# Revit family: 306_34114f9fdf534e40a827953aae8bd5
name_source: partatom
category: Pipe Accessories
units: mm (PartAtom-declared; Revit-internal decimal feet)

## family parameters
Always vertical = Yes
Cut with Voids When Loaded = No
Part Type = Valve - Breaks Into
Round Connector Dimension = Use Diameter
Shared = No
Work Plane-Based = No

## types (22) — shared parameters
Description = 2-way Control valve VLC125, PN25 flange
L2D_Min = 3048 mm
Manufacturer = ESBE
QmdConnectorList = 301;D;302;D
R9 = 4 mm  [stored 0.0131234 ft]
URL = http://www.esbe.eu
X1 = 2 mm  [stored 0.00656168 ft]
Z10 = 3 mm  [stored 0.00984252 ft]
Z14 = 2 mm  [stored 0.00656168 ft]
Z14__ve = -2 mm  [stored -0.00656168 ft]
Z4 = 14 mm  [stored 0.0459318 ft]
Z5 = 7 mm  [stored 0.0229659 ft]
Z6 = 10 mm  [stored 0.0328084 ft]
Z7 = 3 mm  [stored 0.00984252 ft]
Z8 = 15 mm  [stored 0.0492126 ft]
Z9 = 7 mm  [stored 0.0229659 ft]
magiPartTypeId = 306
magiProductFamilyId = 34114f9fdf534e40a827953aae8bd5

## per-type parameters (varying)
- VLC125 PN25 FLANGE DN15-0,25: B1=95 mm; CenSd_R6_6=11 mm; D=15 mm; D2=32 mm; D3=26 mm; D4=22 mm  [stored 0.0721785 ft]; FDT2=48 mm; H3=37 mm; H4=81 mm; HCDT2=22 mm  [stored 0.0721785 ft]; L2D=130 mm; LT2=65 mm; R1=13 mm; R3=24 mm; R4=19 mm; R5=15 mm  [stored 0.0492126 ft]; R6=13 mm; R7=8 mm  [stored 0.0262467 ft]; R8=6 mm  [stored 0.019685 ft]; RD=27 mm; W2D=15 mm  [stored 0.0492126 ft]; X2=10 mm  [stored 0.0328084 ft]; X2__ve=-10 mm  [stored -0.0328084 ft]; Z12=25 mm  [stored 0.082021 ft]; Z12__ve=-25 mm; Z13=4 mm  [stored 0.0131234 ft]; Z15=13 mm; Z3=81 mm; magiProductId=a7967f2f50ef438abf5c4498b49ac1
- VLC125 PN25 FLANGE DN50-38: B1=170 mm; CenSd_R6_6=20 mm  [stored 0.0656168 ft]; D=50 mm; D2=57 mm; D3=53 mm; D4=45 mm; FDT2=83 mm; H3=75 mm; H4=111 mm; HCDT2=48 mm; L2D=230 mm; LT2=115 mm; R1=29 mm; R3=42 mm; R4=34 mm; R5=27 mm; R6=23 mm; R7=14 mm  [stored 0.0459318 ft]; R8=10 mm  [stored 0.0328084 ft]; RD=48 mm; W2D=50 mm; X2=18 mm; X2__ve=-18 mm; Z12=45 mm; Z12__ve=-45 mm; Z13=6 mm  [stored 0.019685 ft]; Z15=26 mm; Z3=126 mm; magiProductId=dca4e9d6c8434ab3bcdf6bdf67ecb1
- VLC125 PN25 FLANGE DN40-6,3: B1=147 mm; CenSd_R6_6=17 mm; D=40 mm; D2=49 mm; D3=46 mm; D4=39 mm; FDT2=75 mm; H3=60 mm; H4=99 mm; HCDT2=41 mm; L2D=200 mm; LT2=100 mm; R1=24 mm; R3=37 mm; R4=29 mm; R5=24 mm; R6=20 mm  [stored 0.0656168 ft]; R7=12 mm  [stored 0.0393701 ft]; R8=9 mm  [stored 0.0295276 ft]; RD=42 mm; W2D=40 mm; X2=16 mm; X2__ve=-16 mm; Z12=39 mm; Z12__ve=-39 mm; Z13=5 mm  [stored 0.0164042 ft]; Z15=21 mm; Z3=106 mm; magiProductId=8e715025a1884100bda2596bc0265d
- VLC125 PN25 FLANGE DN40-4,0: B1=147 mm; CenSd_R6_6=17 mm; D=40 mm; D2=49 mm; D3=46 mm; D4=39 mm; FDT2=75 mm; H3=60 mm; H4=99 mm; HCDT2=41 mm; L2D=200 mm; LT2=100 mm; R1=24 mm; R3=37 mm; R4=29 mm; R5=24 mm; R6=20 mm  [stored 0.0656168 ft]; R7=12 mm  [stored 0.0393701 ft]; R8=9 mm  [stored 0.0295276 ft]; RD=42 mm; W2D=40 mm; X2=16 mm; X2__ve=-16 mm; Z12=39 mm; Z12__ve=-39 mm; Z13=5 mm  [stored 0.0164042 ft]; Z15=21 mm; Z3=106 mm; magiProductId=24df891d75aa46878e8ecd3a11c2c2
- VLC125 PN25 FLANGE DN40-25: B1=147 mm; CenSd_R6_6=17 mm; D=40 mm; D2=49 mm; D3=46 mm; D4=39 mm; FDT2=75 mm; H3=60 mm; H4=99 mm; HCDT2=41 mm; L2D=200 mm; LT2=100 mm; R1=24 mm; R3=37 mm; R4=29 mm; R5=24 mm; R6=20 mm  [stored 0.0656168 ft]; R7=12 mm  [stored 0.0393701 ft]; R8=9 mm  [stored 0.0295276 ft]; RD=42 mm; W2D=40 mm; X2=16 mm; X2__ve=-16 mm; Z12=39 mm; Z12__ve=-39 mm; Z13=5 mm  [stored 0.0164042 ft]; Z15=21 mm; Z3=106 mm; magiProductId=59172ff78d1147d589b4fad22d6343
- VLC125 PN25 FLANGE DN40-2,5: B1=147 mm; CenSd_R6_6=17 mm; D=40 mm; D2=49 mm; D3=46 mm; D4=39 mm; FDT2=75 mm; H3=60 mm; H4=99 mm; HCDT2=41 mm; L2D=200 mm; LT2=100 mm; R1=24 mm; R3=37 mm; R4=29 mm; R5=24 mm; R6=20 mm  [stored 0.0656168 ft]; R7=12 mm  [stored 0.0393701 ft]; R8=9 mm  [stored 0.0295276 ft]; RD=42 mm; W2D=40 mm; X2=16 mm; X2__ve=-16 mm; Z12=39 mm; Z12__ve=-39 mm; Z13=5 mm  [stored 0.0164042 ft]; Z15=21 mm; Z3=106 mm; magiProductId=3eb2a75375fb45ec99bc5d230b8437
- VLC125 PN25 FLANGE DN40-16: B1=147 mm; CenSd_R6_6=17 mm; D=40 mm; D2=49 mm; D3=46 mm; D4=39 mm; FDT2=75 mm; H3=60 mm; H4=99 mm; HCDT2=41 mm; L2D=200 mm; LT2=100 mm; R1=24 mm; R3=37 mm; R4=29 mm; R5=24 mm; R6=20 mm  [stored 0.0656168 ft]; R7=12 mm  [stored 0.0393701 ft]; R8=9 mm  [stored 0.0295276 ft]; RD=42 mm; W2D=40 mm; X2=16 mm; X2__ve=-16 mm; Z12=39 mm; Z12__ve=-39 mm; Z13=5 mm  [stored 0.0164042 ft]; Z15=21 mm; Z3=106 mm; magiProductId=586e9890fe1f49818176a67164677d
- VLC125 PN25 FLANGE DN40-10: B1=147 mm; CenSd_R6_6=17 mm; D=40 mm; D2=49 mm; D3=46 mm; D4=39 mm; FDT2=75 mm; H3=60 mm; H4=99 mm; HCDT2=41 mm; L2D=200 mm; LT2=100 mm; R1=24 mm; R3=37 mm; R4=29 mm; R5=24 mm; R6=20 mm  [stored 0.0656168 ft]; R7=12 mm  [stored 0.0393701 ft]; R8=9 mm  [stored 0.0295276 ft]; RD=42 mm; W2D=40 mm; X2=16 mm; X2__ve=-16 mm; Z12=39 mm; Z12__ve=-39 mm; Z13=5 mm  [stored 0.0164042 ft]; Z15=21 mm; Z3=106 mm; magiProductId=78396739b8a240d9ab94c689cc01a0
- VLC125 PN25 FLANGE DN40-1,6: B1=147 mm; CenSd_R6_6=17 mm; D=40 mm; D2=49 mm; D3=46 mm; D4=39 mm; FDT2=75 mm; H3=60 mm; H4=99 mm; HCDT2=41 mm; L2D=200 mm; LT2=100 mm; R1=24 mm; R3=37 mm; R4=29 mm; R5=24 mm; R6=20 mm  [stored 0.0656168 ft]; R7=12 mm  [stored 0.0393701 ft]; R8=9 mm  [stored 0.0295276 ft]; RD=42 mm; W2D=40 mm; X2=16 mm; X2__ve=-16 mm; Z12=39 mm; Z12__ve=-39 mm; Z13=5 mm  [stored 0.0164042 ft]; Z15=21 mm; Z3=106 mm; magiProductId=13ee520d6b004425beb16537c9af0b
- VLC125 PN25 FLANGE DN32-16: B1=132 mm; CenSd_R6_6=15 mm  [stored 0.0492126 ft]; D=32 mm; D2=44 mm; D3=41 mm; D4=34 mm; FDT2=70 mm; H3=58 mm; H4=100 mm; HCDT2=36 mm; L2D=180 mm; LT2=90 mm; R1=21 mm; R3=33 mm; R4=26 mm; R5=21 mm; R6=18 mm; R7=11 mm; R8=8 mm  [stored 0.0262467 ft]; RD=37 mm; W2D=32 mm; X2=14 mm  [stored 0.0459318 ft]; X2__ve=-14 mm; Z12=35 mm; Z12__ve=-35 mm; Z13=5 mm  [stored 0.0164042 ft]; Z15=20 mm  [stored 0.0656168 ft]; Z3=109 mm; magiProductId=71f0a763826a4e43beadbaa9806b5a
- VLC125 PN25 FLANGE DN25-6,3: B1=117 mm; CenSd_R6_6=14 mm  [stored 0.0459318 ft]; D=25 mm; D2=39 mm; D3=36 mm; D4=30 mm  [stored 0.0984252 ft]; FDT2=58 mm; H3=45 mm; H4=96 mm; HCDT2=32 mm; L2D=160 mm; LT2=80 mm; R1=19 mm; R3=29 mm; R4=23 mm; R5=19 mm; R6=16 mm; R7=9 mm  [stored 0.0295276 ft]; R8=7 mm  [stored 0.0229659 ft]; RD=33 mm; W2D=25 mm  [stored 0.082021 ft]; X2=12 mm  [stored 0.0393701 ft]; X2__ve=-12 mm; Z12=31 mm; Z12__ve=-31 mm; Z13=5 mm  [stored 0.0164042 ft]; Z15=16 mm; Z3=96 mm; magiProductId=38c474cc3f6442a1a0f8b7c69e9160
- VLC125 PN25 FLANGE DN25-4,0: B1=117 mm; CenSd_R6_6=14 mm  [stored 0.0459318 ft]; D=25 mm; D2=39 mm; D3=36 mm; D4=30 mm  [stored 0.0984252 ft]; FDT2=58 mm; H3=45 mm; H4=96 mm; HCDT2=32 mm; L2D=160 mm; LT2=80 mm; R1=19 mm; R3=29 mm; R4=23 mm; R5=19 mm; R6=16 mm; R7=9 mm  [stored 0.0295276 ft]; R8=7 mm  [stored 0.0229659 ft]; RD=33 mm; W2D=25 mm  [stored 0.082021 ft]; X2=12 mm  [stored 0.0393701 ft]; X2__ve=-12 mm; Z12=31 mm; Z12__ve=-31 mm; Z13=5 mm  [stored 0.0164042 ft]; Z15=16 mm; Z3=96 mm; magiProductId=9c515ab929be47d0a735c42dc62332
- VLC125 PN25 FLANGE DN25-2,5: B1=117 mm; CenSd_R6_6=14 mm  [stored 0.0459318 ft]; D=25 mm; D2=39 mm; D3=36 mm; D4=30 mm  [stored 0.0984252 ft]; FDT2=58 mm; H3=45 mm; H4=96 mm; HCDT2=32 mm; L2D=160 mm; LT2=80 mm; R1=19 mm; R3=29 mm; R4=23 mm; R5=19 mm; R6=16 mm; R7=9 mm  [stored 0.0295276 ft]; R8=7 mm  [stored 0.0229659 ft]; RD=33 mm; W2D=25 mm  [stored 0.082021 ft]; X2=12 mm  [stored 0.0393701 ft]; X2__ve=-12 mm; Z12=31 mm; Z12__ve=-31 mm; Z13=5 mm  [stored 0.0164042 ft]; Z15=16 mm; Z3=96 mm; magiProductId=006b1c5775c34ee8b07f227e318cdb
- VLC125 PN25 FLANGE DN25-10: B1=117 mm; CenSd_R6_6=14 mm  [stored 0.0459318 ft]; D=25 mm; D2=39 mm; D3=36 mm; D4=30 mm  [stored 0.0984252 ft]; FDT2=58 mm; H3=45 mm; H4=96 mm; HCDT2=32 mm; L2D=160 mm; LT2=80 mm; R1=19 mm; R3=29 mm; R4=23 mm; R5=19 mm; R6=16 mm; R7=9 mm  [stored 0.0295276 ft]; R8=7 mm  [stored 0.0229659 ft]; RD=33 mm; W2D=25 mm  [stored 0.082021 ft]; X2=12 mm  [stored 0.0393701 ft]; X2__ve=-12 mm; Z12=31 mm; Z12__ve=-31 mm; Z13=5 mm  [stored 0.0164042 ft]; Z15=16 mm; Z3=96 mm; magiProductId=6a42770237cd4d328b9c5f8a9aa48a
- VLC125 PN25 FLANGE DN25-1,6: B1=117 mm; CenSd_R6_6=14 mm  [stored 0.0459318 ft]; D=25 mm; D2=39 mm; D3=36 mm; D4=30 mm  [stored 0.0984252 ft]; FDT2=58 mm; H3=45 mm; H4=96 mm; HCDT2=32 mm; L2D=160 mm; LT2=80 mm; R1=19 mm; R3=29 mm; R4=23 mm; R5=19 mm; R6=16 mm; R7=9 mm  [stored 0.0295276 ft]; R8=7 mm  [stored 0.0229659 ft]; RD=33 mm; W2D=25 mm  [stored 0.082021 ft]; X2=12 mm  [stored 0.0393701 ft]; X2__ve=-12 mm; Z12=31 mm; Z12__ve=-31 mm; Z13=5 mm  [stored 0.0164042 ft]; Z15=16 mm; Z3=96 mm; magiProductId=71af0ebcfd99460e8bd11ee4716e5f
- VLC125 PN25 FLANGE DN20-6,3: B1=110 mm; CenSd_R6_6=13 mm; D=20 mm; D2=37 mm; D3=31 mm; D4=26 mm; FDT2=53 mm; H3=40 mm; H4=92 mm; HCDT2=27 mm; L2D=150 mm; LT2=75 mm; R1=16 mm; R3=27 mm; R4=22 mm  [stored 0.0721785 ft]; R5=18 mm; R6=15 mm  [stored 0.0492126 ft]; R7=9 mm  [stored 0.0295276 ft]; R8=7 mm  [stored 0.0229659 ft]; RD=31 mm; W2D=20 mm  [stored 0.0656168 ft]; X2=12 mm  [stored 0.0393701 ft]; X2__ve=-12 mm; Z12=29 mm; Z12__ve=-29 mm  [stored -0.0951444 ft]; Z13=5 mm  [stored 0.0164042 ft]; Z15=14 mm  [stored 0.0459318 ft]; Z3=90 mm; magiProductId=a2b5603518e44335b34ca23d5a057e
- VLC125 PN25 FLANGE DN15-4,0: B1=95 mm; CenSd_R6_6=11 mm; D=15 mm; D2=32 mm; D3=26 mm; D4=22 mm  [stored 0.0721785 ft]; FDT2=48 mm; H3=37 mm; H4=81 mm; HCDT2=22 mm  [stored 0.0721785 ft]; L2D=130 mm; LT2=65 mm; R1=13 mm; R3=24 mm; R4=19 mm; R5=15 mm  [stored 0.0492126 ft]; R6=13 mm; R7=8 mm  [stored 0.0262467 ft]; R8=6 mm  [stored 0.019685 ft]; RD=27 mm; W2D=15 mm  [stored 0.0492126 ft]; X2=10 mm  [stored 0.0328084 ft]; X2__ve=-10 mm  [stored -0.0328084 ft]; Z12=25 mm  [stored 0.082021 ft]; Z12__ve=-25 mm; Z13=4 mm  [stored 0.0131234 ft]; Z15=13 mm; Z3=81 mm; magiProductId=82762e9d86334c45a5479a56c473d2
- VLC125 PN25 FLANGE DN15-2,5: B1=95 mm; CenSd_R6_6=11 mm; D=15 mm; D2=32 mm; D3=26 mm; D4=22 mm  [stored 0.0721785 ft]; FDT2=48 mm; H3=37 mm; H4=81 mm; HCDT2=22 mm  [stored 0.0721785 ft]; L2D=130 mm; LT2=65 mm; R1=13 mm; R3=24 mm; R4=19 mm; R5=15 mm  [stored 0.0492126 ft]; R6=13 mm; R7=8 mm  [stored 0.0262467 ft]; R8=6 mm  [stored 0.019685 ft]; RD=27 mm; W2D=15 mm  [stored 0.0492126 ft]; X2=10 mm  [stored 0.0328084 ft]; X2__ve=-10 mm  [stored -0.0328084 ft]; Z12=25 mm  [stored 0.082021 ft]; Z12__ve=-25 mm; Z13=4 mm  [stored 0.0131234 ft]; Z15=13 mm; Z3=81 mm; magiProductId=6c694fafdb71441badeec607fc738e
- VLC125 PN25 FLANGE DN15-1,6: B1=95 mm; CenSd_R6_6=11 mm; D=15 mm; D2=32 mm; D3=26 mm; D4=22 mm  [stored 0.0721785 ft]; FDT2=48 mm; H3=37 mm; H4=81 mm; HCDT2=22 mm  [stored 0.0721785 ft]; L2D=130 mm; LT2=65 mm; R1=13 mm; R3=24 mm; R4=19 mm; R5=15 mm  [stored 0.0492126 ft]; R6=13 mm; R7=8 mm  [stored 0.0262467 ft]; R8=6 mm  [stored 0.019685 ft]; RD=27 mm; W2D=15 mm  [stored 0.0492126 ft]; X2=10 mm  [stored 0.0328084 ft]; X2__ve=-10 mm  [stored -0.0328084 ft]; Z12=25 mm  [stored 0.082021 ft]; Z12__ve=-25 mm; Z13=4 mm  [stored 0.0131234 ft]; Z15=13 mm; Z3=81 mm; magiProductId=a4ff239629e14974815f24e1197d05
- VLC125 PN25 FLANGE DN15-1,0: B1=95 mm; CenSd_R6_6=11 mm; D=15 mm; D2=32 mm; D3=26 mm; D4=22 mm  [stored 0.0721785 ft]; FDT2=48 mm; H3=37 mm; H4=81 mm; HCDT2=22 mm  [stored 0.0721785 ft]; L2D=130 mm; LT2=65 mm; R1=13 mm; R3=24 mm; R4=19 mm; R5=15 mm  [stored 0.0492126 ft]; R6=13 mm; R7=8 mm  [stored 0.0262467 ft]; R8=6 mm  [stored 0.019685 ft]; RD=27 mm; W2D=15 mm  [stored 0.0492126 ft]; X2=10 mm  [stored 0.0328084 ft]; X2__ve=-10 mm  [stored -0.0328084 ft]; Z12=25 mm  [stored 0.082021 ft]; Z12__ve=-25 mm; Z13=4 mm  [stored 0.0131234 ft]; Z15=13 mm; Z3=81 mm; magiProductId=324fe785cce345c5a2744de3ac29c6
- VLC125 PN25 FLANGE DN15-0,63: B1=95 mm; CenSd_R6_6=11 mm; D=15 mm; D2=32 mm; D3=26 mm; D4=22 mm  [stored 0.0721785 ft]; FDT2=48 mm; H3=37 mm; H4=81 mm; HCDT2=22 mm  [stored 0.0721785 ft]; L2D=130 mm; LT2=65 mm; R1=13 mm; R3=24 mm; R4=19 mm; R5=15 mm  [stored 0.0492126 ft]; R6=13 mm; R7=8 mm  [stored 0.0262467 ft]; R8=6 mm  [stored 0.019685 ft]; RD=27 mm; W2D=15 mm  [stored 0.0492126 ft]; X2=10 mm  [stored 0.0328084 ft]; X2__ve=-10 mm  [stored -0.0328084 ft]; Z12=25 mm  [stored 0.082021 ft]; Z12__ve=-25 mm; Z13=4 mm  [stored 0.0131234 ft]; Z15=13 mm; Z3=81 mm; magiProductId=886fbcb2a3464bd3b9ddb9dde10590
- VLC125 PN25 FLANGE DN15-0,4: B1=95 mm; CenSd_R6_6=11 mm; D=15 mm; D2=32 mm; D3=26 mm; D4=22 mm  [stored 0.0721785 ft]; FDT2=48 mm; H3=37 mm; H4=81 mm; HCDT2=22 mm  [stored 0.0721785 ft]; L2D=130 mm; LT2=65 mm; R1=13 mm; R3=24 mm; R4=19 mm; R5=15 mm  [stored 0.0492126 ft]; R6=13 mm; R7=8 mm  [stored 0.0262467 ft]; R8=6 mm  [stored 0.019685 ft]; RD=27 mm; W2D=15 mm  [stored 0.0492126 ft]; X2=10 mm  [stored 0.0328084 ft]; X2__ve=-10 mm  [stored -0.0328084 ft]; Z12=25 mm  [stored 0.082021 ft]; Z12__ve=-25 mm; Z13=4 mm  [stored 0.0131234 ft]; Z15=13 mm; Z3=81 mm; magiProductId=a2146959273e4461aed8da9f6f7584

note: column(s) folded — value = type name in every type: magiProductCode

note: [stored X ft] marks values corroborated as IEEE doubles in the binary element streams (Revit-internal decimal feet)

## geometry (parser evidence)
native form markers: Sweep x3
no freeform markers — native parametric forms only
